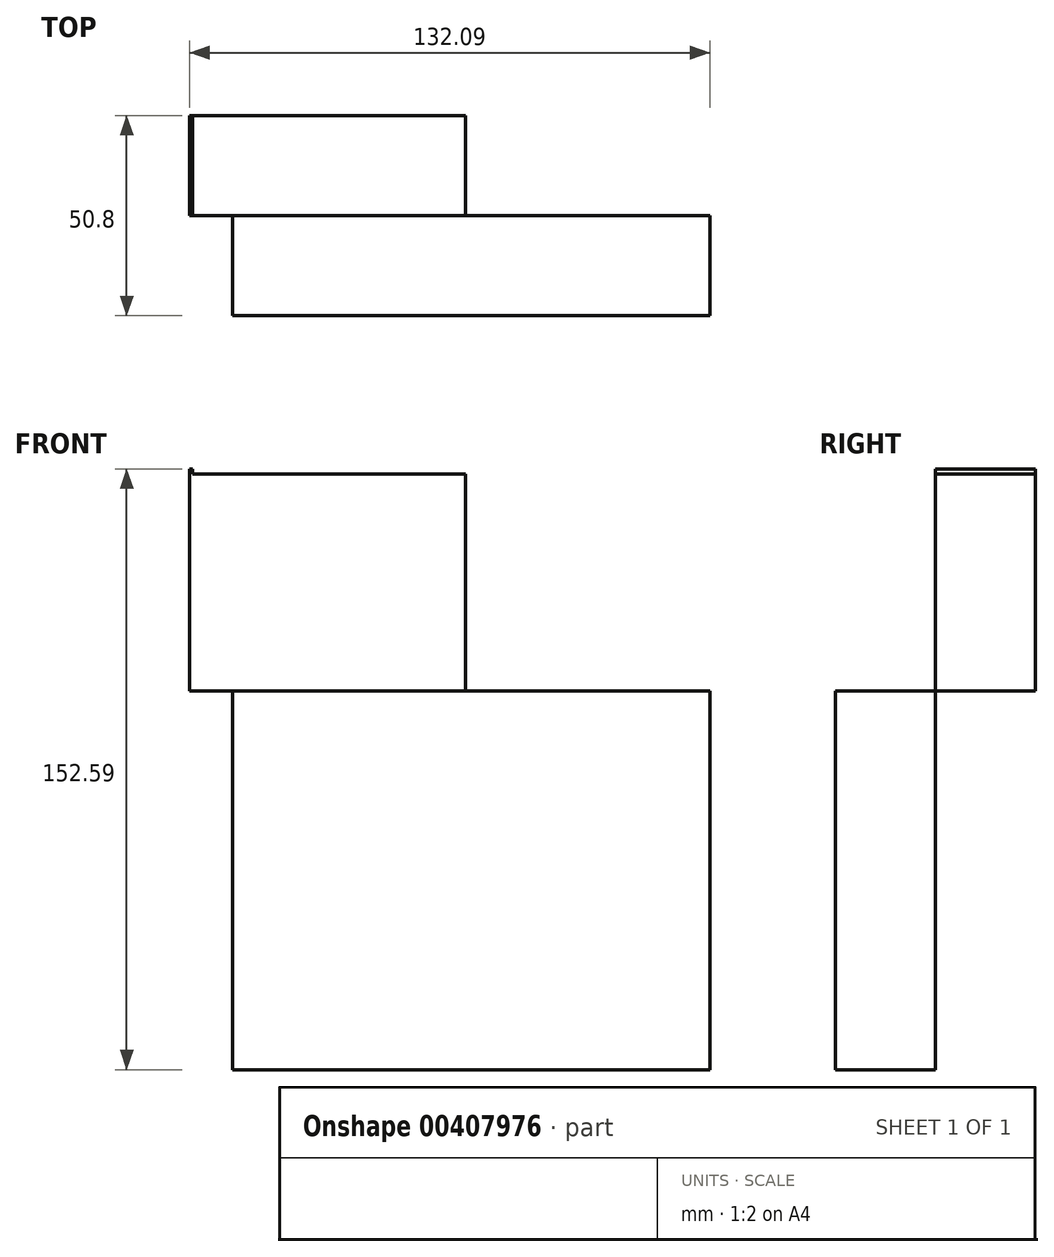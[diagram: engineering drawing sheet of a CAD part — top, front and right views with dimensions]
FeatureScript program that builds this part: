
annotation { "Feature Type Name" : "Feature", "Feature Type Description" : "" }
export const myFeature = defineFeature(function(context is Context, id is Id, definition is map)
    precondition{}
    {
        {
            var Q0;
            Q0=qCreatedBy(makeId("Front.planeOp"),FACE);
            var sketch = newSketch(context, id + "F0", { "sketchPlane" : qUnion([Q0])});
            skLineSegment(sketch, "E0.bottom", {"start": v(-69.26, 0) * mm, "end": v(-70, 0) * mm});
            skLineSegment(sketch, "E0.top", {"start": v(-69.26, 56.38) * mm, "end": v(-70, 56.38) * mm});
            skLineSegment(sketch, "E0.left", {"start": v(-69.26, 0) * mm, "end": v(-69.26, 56.38) * mm});
            skLineSegment(sketch, "E0.right", {"start": v(-70, 0) * mm, "end": v(-70, 56.38) * mm});
            skLineSegment(sketch, "E1.bottom", {"start": v(0, 55.08) * mm, "end": v(0, 55.08) * mm});
            skLineSegment(sketch, "E1.top", {"start": v(0, 0) * mm, "end": v(0, 0) * mm});
            skLineSegment(sketch, "E1.left", {"start": v(0, 55.08) * mm, "end": v(0, 0) * mm});
            skLineSegment(sketch, "E1.right", {"start": v(0, 55.08) * mm, "end": v(0, 0) * mm});
            skLineSegment(sketch, "E2.bottom", {"start": v(-69.26, 0) * mm, "end": v(0, 0) * mm});
            skLineSegment(sketch, "E2.top", {"start": v(-69.26, 55.08) * mm, "end": v(0, 55.08) * mm});
            skLineSegment(sketch, "E2.left", {"start": v(-69.26, 0) * mm, "end": v(-69.26, 55.08) * mm});
            skLineSegment(sketch, "E2.right", {"start": v(0, 0) * mm, "end": v(0, 55.08) * mm});
            skSolve(sketch);
        }
        {
            var Q0;
            Q0 = qSketchRegion(id + "F0", true);
            extrude(context, id + "F1", {"entities" : qUnion([Q0]), "depth" : 25.4 * mm});
        }
        {
            var Q0;
            Q0=makeQuery(id+"F1.opExtrude","CAP_FACE",FACE,{"disambiguationData":[OSD([sQuery(id+"F0.wireOp",EDGE,"E0.bottom"),sQuery(id+"F0.wireOp",EDGE,"E0.top"),sQuery(id+"F0.wireOp",EDGE,"E0.left"),sQuery(id+"F0.wireOp",EDGE,"E0.right"),sQuery(id+"F0.wireOp",EDGE,"E2.bottom"),sQuery(id+"F0.wireOp",EDGE,"E2.top"),sQuery(id+"F0.wireOp",EDGE,"E2.right")])],"isStart":false});
            var sketch = newSketch(context, id + "F2", { "sketchPlane" : qUnion([Q0])});
            skLineSegment(sketch, "E3.bottom", {"start": v(52.52, 32.07) * mm, "end": v(17.32, 32.07) * mm});
            skLineSegment(sketch, "E3.top", {"start": v(52.52, 81.52) * mm, "end": v(17.32, 81.52) * mm});
            skLineSegment(sketch, "E3.left", {"start": v(52.52, 32.07) * mm, "end": v(52.52, 81.52) * mm});
            skLineSegment(sketch, "E3.right", {"start": v(17.32, 32.07) * mm, "end": v(17.32, 81.52) * mm});
            skLineSegment(sketch, "E4.bottom", {"start": v(-59.12, -96.2) * mm, "end": v(62.1, -96.2) * mm});
            skLineSegment(sketch, "E4.top", {"start": v(-59.12, 0) * mm, "end": v(62.1, 0) * mm});
            skLineSegment(sketch, "E4.left", {"start": v(-59.12, -96.2) * mm, "end": v(-59.12, 0) * mm});
            skLineSegment(sketch, "E4.right", {"start": v(62.1, -96.2) * mm, "end": v(62.1, 0) * mm});
            skSolve(sketch);
        }
        {
            var Q0;
            Q0=makeQuery(id+"F2.imprint","IMPRINT",FACE,{"disambiguationData":[TD([[makeQuery(id+"F2.imprint","IMPRINT",EDGE,{"derivedFrom":sQuery(id+"F2.wireOp",EDGE,"E4.bottom")}),1.0]])]});
            var sketch = newSketch(context, id + "F3", { "sketchPlane" : qUnion([Q0])});
            skSolve(sketch);
        }
        {
            var Q0;
            Q0=makeQuery(id+"F3.imprint","IMPRINT",FACE,{"disambiguationData":[TD([[makeQuery(id+"F3.imprint","IMPRINT",EDGE,{"derivedFrom":makeQuery(id+"F2.imprint","IMPRINT",EDGE,{"derivedFrom":sQuery(id+"F2.wireOp",EDGE,"E4.bottom")})}),1.0]])]});
            extrude(context, id + "F4", {"entities" : qUnion([Q0]), "depth" : 25.4 * mm});
        }
    });
